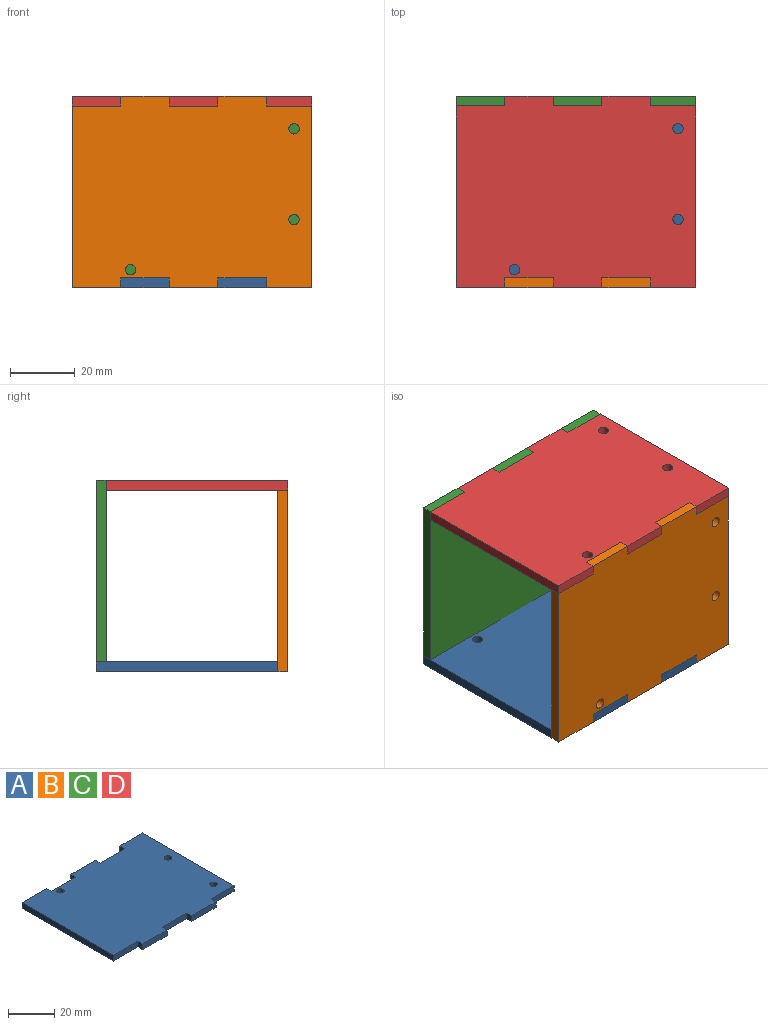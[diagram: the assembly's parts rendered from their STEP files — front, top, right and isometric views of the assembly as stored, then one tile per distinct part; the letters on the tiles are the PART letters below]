
ASSEMBLY  parts=4 mates=3
PART A: 25 faces, bbox 74x59x3 mm
  f0: plane 56x3mm, normal (-1,0,0), area 168mm2, adj f1,f22,f23,f24
  f1: plane 15x3mm, normal (0,-1,0), area 45mm2, adj f0,f2,f23,f24
  f2: plane 3x3mm, normal (-1,0,0), area 9mm2, adj f1,f3,f23,f24
  f3: plane 15x3mm, normal (0,-1,0), area 45mm2, adj f2,f4,f23,f24
  f4: plane 3x3mm, normal (1,0,0), area 9mm2, adj f3,f5,f23,f24
  f5: plane 15x3mm, normal (0,-1,0), area 45mm2, adj f4,f6,f23,f24
  f6: plane 3x3mm, normal (-1,0,0), area 9mm2, adj f5,f7,f23,f24
  f7: plane 15x3mm, normal (0,-1,0), area 45mm2, adj f6,f8,f23,f24
  f8: plane 3x3mm, normal (1,0,0), area 9mm2, adj f7,f9,f23,f24
  f9: plane 14x3mm, normal (0,-1,0), area 42mm2, adj f8,f10,f23,f24
  f10: plane 56x3mm, normal (1,0,0), area 168mm2, adj f9,f11,f23,f24
  f11: plane 14x3mm, normal (0,1,0), area 42mm2, adj f10,f12,f23,f24
  f12: plane 3x3mm, normal (-1,0,0), area 9mm2, adj f11,f13,f23,f24
  f13: plane 15x3mm, normal (0,1,0), area 45mm2, adj f12,f14,f23,f24
  f14: plane 3x3mm, normal (1,0,0), area 9mm2, adj f13,f15,f23,f24
  f15: plane 15x3mm, normal (0,1,0), area 45mm2, adj f14,f16,f23,f24
  f16: plane 3x3mm, normal (-1,0,0), area 9mm2, adj f15,f17,f23,f24
  f17: plane 15x3mm, normal (0,1,0), area 45mm2, adj f16,f18,f23,f24
  f18: plane 3x3mm, normal (1,0,0), area 9mm2, adj f17,f22,f23,f24
  f19: cylinder r=1.6mm len=3.2mm, axis (0,0,-1), area 30.2mm2, adj f23,f24
  f20: cylinder r=1.6mm len=3.2mm, axis (0,0,-1), area 30.2mm2, adj f23,f24
  f21: cylinder r=1.6mm len=3.2mm, axis (0,0,-1), area 30.2mm2, adj f23,f24
  f22: plane 15x3mm, normal (0,1,0), area 45mm2, adj f0,f18,f23,f24
  f23: plane 74x59mm, normal (0,0,1), area 4119.9mm2, adj f0,f1,f2,f3,f4,f5,f6,f7
  f24: plane 74x59mm, normal (0,0,-1), area 4119.9mm2, adj f0,f1,f2,f3,f4,f5,f6,f7
PART B: same geometry as A
PART C: same geometry as A
PART D: same geometry as A
PLACE A t=(-18.19,7.64,-5.78)mm
PLACE B rot(axis=(-1,0,0),90deg) t=(-18.19,-21.86,23.72)mm
PLACE C rot(axis=(1,0,0),90deg) t=(-18.19,37.14,23.72)mm
PLACE D rot(axis=(-1,0,0),180deg) t=(-18.19,7.64,53.22)mm
MATE fastened B.f8 <-> D.f12  axis (1,0,0) through (4.81,-20.36,51.72)mm
MATE fastened B.f12 <-> A.f8  axis (-1,0,0) through (4.81,-20.36,-4.28)mm
MATE fastened D.f2 <-> C.f18  axis (-1,0,0) through (-40.19,35.64,51.72)mm
